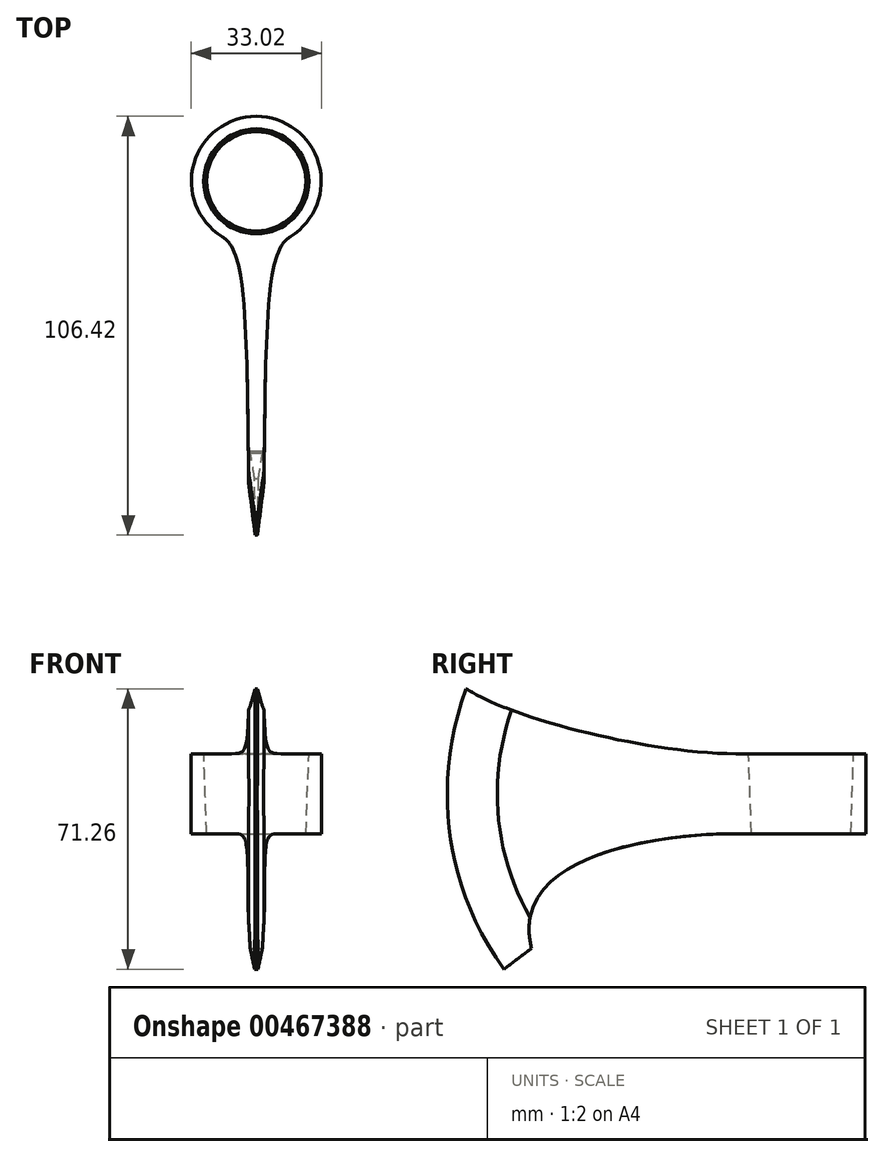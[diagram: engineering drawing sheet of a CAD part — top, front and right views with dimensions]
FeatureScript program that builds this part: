
annotation { "Feature Type Name" : "Feature", "Feature Type Description" : "" }
export const myFeature = defineFeature(function(context is Context, id is Id, definition is map)
    precondition{}
    {
        {
            var Q0;
            Q0=qCreatedBy(makeId("Right.planeOp"),FACE);
            var sketch = newSketch(context, id + "F0", { "sketchPlane" : qUnion([Q0])});
            skLineSegment(sketch, "E0", {"start": v(0, 0) * mm, "end": v(0, 76.51) * mm, "construction": true});
            skLineSegment(sketch, "E1", {"start": v(0, 0) * mm, "end": v(0, -76.51) * mm, "construction": true});
            skLineSegment(sketch, "E2.bottom", {"start": v(-16.51, 10.16) * mm, "end": v(16.51, 10.16) * mm});
            skLineSegment(sketch, "E2.top", {"start": v(-16.51, -10.16) * mm, "end": v(16.5, -10.16) * mm});
            skLineSegment(sketch, "E2.left", {"start": v(-16.51, 10.16) * mm, "end": v(-16.51, -10.16) * mm});
            skLineSegment(sketch, "E2.right", {"start": v(16.51, 10.16) * mm, "end": v(16.51, -10.16) * mm});
            skPoint(sketch, "E2.middle", {"position": v(0, 0) * mm});
            skFitSpline(sketch, "E3", {"points": [v(-85.1, 26.67) * mm, v(-16.51, 10.16) * mm], "startDerivative": vector(34.44, -22.9) * mm, "endDerivative": vector(65.64, 0) * mm});
            skLineSegment(sketch, "E4", {"start": v(0, 0) * mm, "end": v(-85.1, 0) * mm, "construction": true});
            skFitSpline(sketch, "E5.MirrorCS", {"points": [v(-85.1, -26.67) * mm, v(-16.51, -10.16) * mm], "startDerivative": vector(34.44, 22.9) * mm, "endDerivative": vector(65.64, 0) * mm, "construction": true});
            skArc(sketch, "E6", {"start": v(-85.1, 26.67) * mm, "mid": v(-89.23, -10.16) * mm, "end": v(-75.5, -44.59) * mm});
            skLineSegment(sketch, "E7", {"start": v(-75.5, -44.59) * mm, "end": v(-68.48, -39.3) * mm});
            skFitSpline(sketch, "E8", {"points": [v(-16.51, -10.16) * mm, v(-68.48, -39.3) * mm], "startDerivative": vector(-55.5, 0) * mm, "endDerivative": vector(18.63, -72.91) * mm});
            skSolve(sketch);
        }
        {
            var Q0;
            Q0 = qSketchRegion(id + "F0", true);
            extrude(context, id + "F1", {"entities" : qUnion([Q0]), "endBound" : BoundingType.SYMMETRIC, "oppositeDirection" : true, "depth" : 50.8 * mm});
        }
        {
            var Q0;
            Q0=qCreatedBy(makeId("Top.planeOp"),FACE);
            var sketch = newSketch(context, id + "F2", { "sketchPlane" : qUnion([Q0])});
            skPoint(sketch, "E9.0", {"position": v(0, -16.51) * mm});
            skArc(sketch, "E10", {"start": v(0, 16.51) * mm, "mid": v(-15.87, 4.56) * mm, "end": v(-8.76, -14) * mm});
            skLineSegment(sketch, "E11", {"start": v(0, 16.51) * mm, "end": v(0, -117.08) * mm, "construction": true});
            skPoint(sketch, "E12", {"position": v(-1.27, -94.57) * mm});
            skFitSpline(sketch, "E13", {"points": [v(-1.27, -94.57) * mm, v(-4.74, -20.4) * mm, v(-8.76, -14) * mm], "startDerivative": vector(-5.64, 84.29) * mm, "endDerivative": vector(-16.07, 10.07) * mm});
            skLineSegment(sketch, "E14", {"start": v(0, -94.57) * mm, "end": v(-1.27, -94.57) * mm});
            skArc(sketch, "E15.MirrorCS", {"start": v(0, 16.51) * mm, "mid": v(15.87, 4.56) * mm, "end": v(8.76, -14) * mm});
            skFitSpline(sketch, "E16.MirrorCS", {"points": [v(1.27, -94.57) * mm, v(4.74, -20.4) * mm, v(8.76, -14) * mm], "startDerivative": vector(5.64, 84.29) * mm, "endDerivative": vector(16.07, 10.07) * mm});
            skLineSegment(sketch, "E17.MirrorCS", {"start": v(0, -94.57) * mm, "end": v(1.27, -94.57) * mm});
            skSolve(sketch);
        }
        {
            var Q0;
            Q0 = qSketchRegion(id + "F2", true);
            extrude(context, id + "F3", {"entities" : qUnion([Q0]), "endBound" : BoundingType.SYMMETRIC, "depth" : 127 * mm});
        }
        {
            var Q0;
            Q0=makeQuery(id+"F1.opExtrude","SWEPT_BODY",BODY,{"disambiguationData":[OSD([sQuery(id+"F0.wireOp",EDGE,"E2.bottom"),sQuery(id+"F0.wireOp",EDGE,"E2.top"),sQuery(id+"F0.wireOp",EDGE,"E2.right"),sQuery(id+"F0.wireOp",EDGE,"E3"),sQuery(id+"F0.wireOp",EDGE,"E6"),sQuery(id+"F0.wireOp",EDGE,"E7"),sQuery(id+"F0.wireOp",EDGE,"E8")])]});
            var Q1;
            Q1=makeQuery(id+"F3.opExtrude","SWEPT_BODY",BODY,{"disambiguationData":[OSD([sQuery(id+"F2.wireOp",EDGE,"E10"),sQuery(id+"F2.wireOp",EDGE,"E13"),sQuery(id+"F2.wireOp",EDGE,"E14"),sQuery(id+"F2.wireOp",EDGE,"E15.MirrorCS"),sQuery(id+"F2.wireOp",EDGE,"E16.MirrorCS"),sQuery(id+"F2.wireOp",EDGE,"E17.MirrorCS")])]});
            booleanBodies(context, id + "F4", {"operationType" : BooleanOperationType.INTERSECTION, "tools" : qUnion([Q0, Q1])});
        }
        {
            var Q0;
            Q0=makeQuery(id+"F1.opExtrude","SWEPT_FACE",FACE,{"disambiguationData":[OSD([sQuery(id+"F0.wireOp",EDGE,"E2.bottom")])]});
            var sketch = newSketch(context, id + "F5", { "sketchPlane" : qUnion([Q0])});
            skCircle(sketch, "E18", {"center": v(0, 0) * mm, "radius": 13.33 * mm});
            skSolve(sketch);
        }
        {
            var Q0;
            Q0 = qSketchRegion(id + "F5", true);
            var Q1;
            Q1=makeQuery(id+"F5.imprint","IMPRINT",FACE,{"disambiguationData":[TD([[makeQuery(id+"F5.imprint","IMPRINT",EDGE,{"derivedFrom":sQuery(id+"F5.wireOp",EDGE,"E18")}),1.0]])]});
            extrude(context, id + "F6", {"entities" : qUnion([Q0, Q1]), "operationType" : NewBodyOperationType.REMOVE, "endBound" : BoundingType.THROUGH_ALL, "oppositeDirection" : true, "depth" : 106.93 * mm, "hasDraft" : true, "draftAngle" : 2 * degree, "draftPullDirection" : true});
        }
        {
            var Q0;
            Q0=makeQuery(id+"F4.opBoolean","INTERSECT",EDGE,{"derivedFrom":[makeQuery(id+"F1.opExtrude","SWEPT_FACE",FACE,{"disambiguationData":[OSD([sQuery(id+"F0.wireOp",EDGE,"E6")])]}),makeQuery(id+"F3.opExtrude","SWEPT_FACE",FACE,{"disambiguationData":[OSD([sQuery(id+"F2.wireOp",EDGE,"E16.MirrorCS")])]})]});
            var Q1;
            Q1=makeQuery(id+"F4.opBoolean","INTERSECT",EDGE,{"derivedFrom":[makeQuery(id+"F1.opExtrude","SWEPT_FACE",FACE,{"disambiguationData":[OSD([sQuery(id+"F0.wireOp",EDGE,"E6")])]}),makeQuery(id+"F3.opExtrude","SWEPT_FACE",FACE,{"disambiguationData":[OSD([sQuery(id+"F2.wireOp",EDGE,"E13")])]})]});
            chamfer(context, id + "F7", {"entities" : qUnion([Q0, Q1]), "chamferType" : ChamferType.TWO_OFFSETS, "width1" : 12.7 * mm, "oppositeDirection" : false, "width2" : 1.27 * mm, "tangentPropagation" : true});
        }
    });
